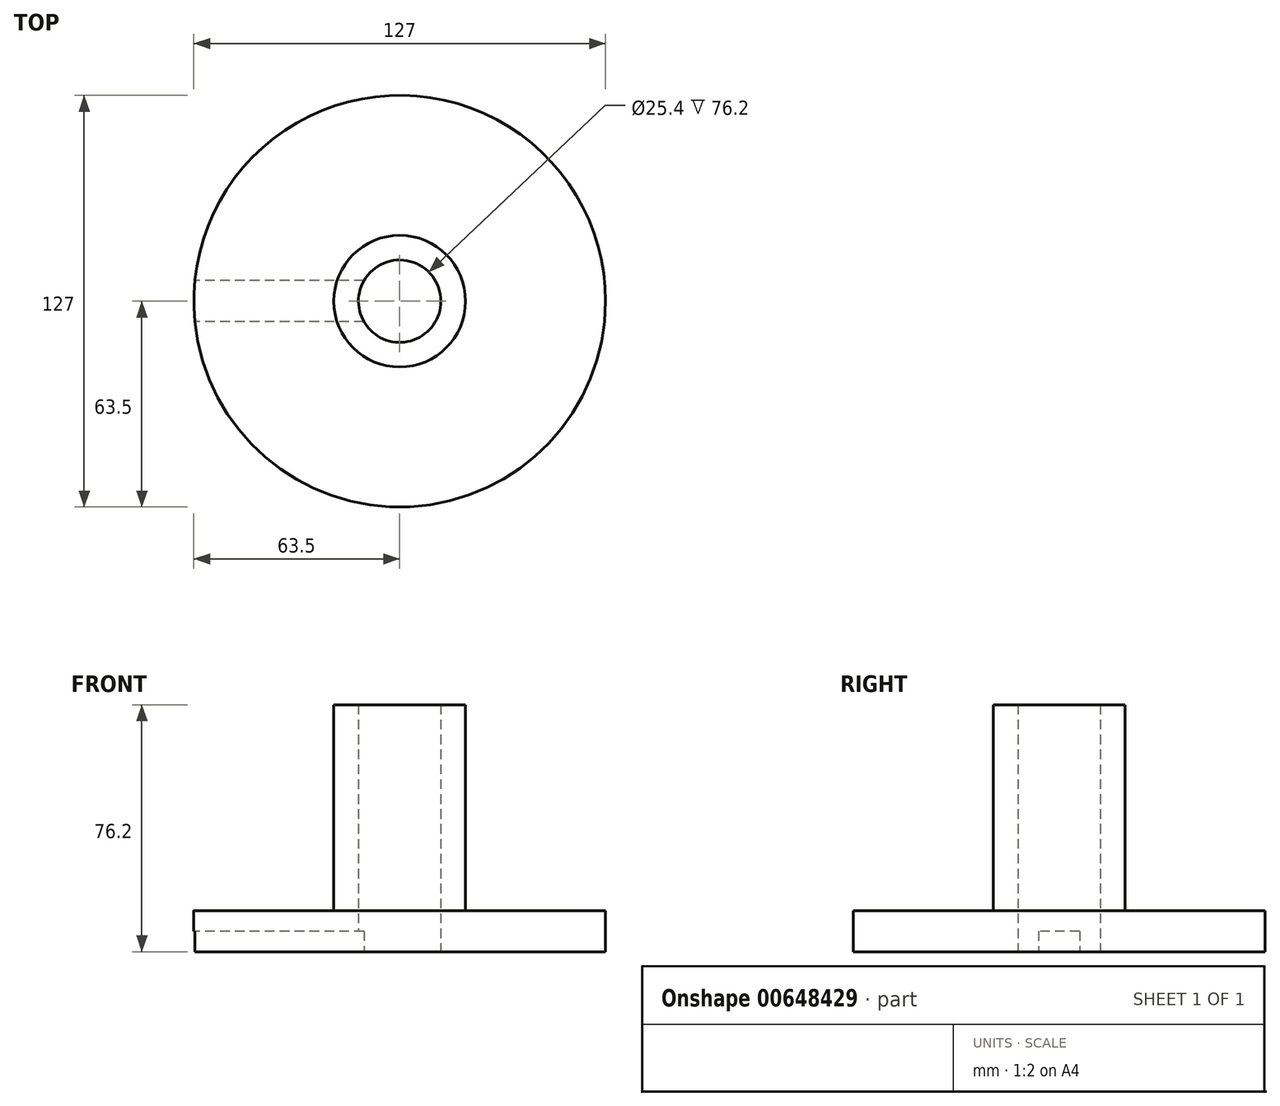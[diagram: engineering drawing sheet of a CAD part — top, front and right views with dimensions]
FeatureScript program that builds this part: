
annotation { "Feature Type Name" : "Feature", "Feature Type Description" : "" }
export const myFeature = defineFeature(function(context is Context, id is Id, definition is map)
    precondition{}
    {
        {
            var Q0;
            Q0=qCreatedBy(makeId("Top.planeOp"),FACE);
            var sketch = newSketch(context, id + "F0", { "sketchPlane" : qUnion([Q0])});
            skCircle(sketch, "E0", {"center": v(0, 0) * mm, "radius": 20.32 * mm});
            skCircle(sketch, "E1", {"center": v(0, 0) * mm, "radius": 12.7 * mm});
            skCircle(sketch, "E2", {"center": v(0, 0) * mm, "radius": 63.5 * mm});
            skSolve(sketch);
        }
        {
            var Q0;
            Q0=makeQuery(id+"F0.imprint","IMPRINT",FACE,{"disambiguationData":[TD([[makeQuery(id+"F0.imprint","IMPRINT",EDGE,{"derivedFrom":sQuery(id+"F0.wireOp",EDGE,"E0")}),-1.0]])]});
            extrude(context, id + "F1", {"entities" : qUnion([Q0]), "depth" : 12.7 * mm, "offsetDistance" : 25.4 * mm});
        }
        {
            var Q0;
            Q0=makeQuery(id+"F0.imprint","IMPRINT",FACE,{"disambiguationData":[TD([[makeQuery(id+"F0.imprint","IMPRINT",EDGE,{"derivedFrom":sQuery(id+"F0.wireOp",EDGE,"E0")}),1.0]])]});
            var Q1;
            Q1=sQuery(id+"F0.wireOp",EDGE,"E0");
            extrude(context, id + "F2", {"entities" : qUnion([Q0]), "operationType" : NewBodyOperationType.ADD, "surfaceEntities" : qUnion([Q1]), "depth" : 76.2 * mm, "offsetDistance" : 25.4 * mm});
        }
        {
            var Q0;
            Q0=qCreatedBy(makeId("Top.planeOp"),FACE);
            var sketch = newSketch(context, id + "F3", { "sketchPlane" : qUnion([Q0])});
            skLineSegment(sketch, "E3.bottom", {"start": v(0, -6.35) * mm, "end": v(-127, -6.35) * mm});
            skLineSegment(sketch, "E3.top", {"start": v(0, 6.35) * mm, "end": v(-127, 6.35) * mm});
            skLineSegment(sketch, "E3.left", {"start": v(0, -6.35) * mm, "end": v(0, 6.35) * mm});
            skLineSegment(sketch, "E3.right", {"start": v(-127, -6.35) * mm, "end": v(-127, 6.35) * mm});
            skSolve(sketch);
        }
        {
            var Q0;
            Q0 = qSketchRegion(id + "F3", true);
            extrude(context, id + "F4", {"entities" : qUnion([Q0]), "operationType" : NewBodyOperationType.REMOVE, "depth" : 6.35 * mm, "offsetDistance" : 25.4 * mm});
        }
    });
